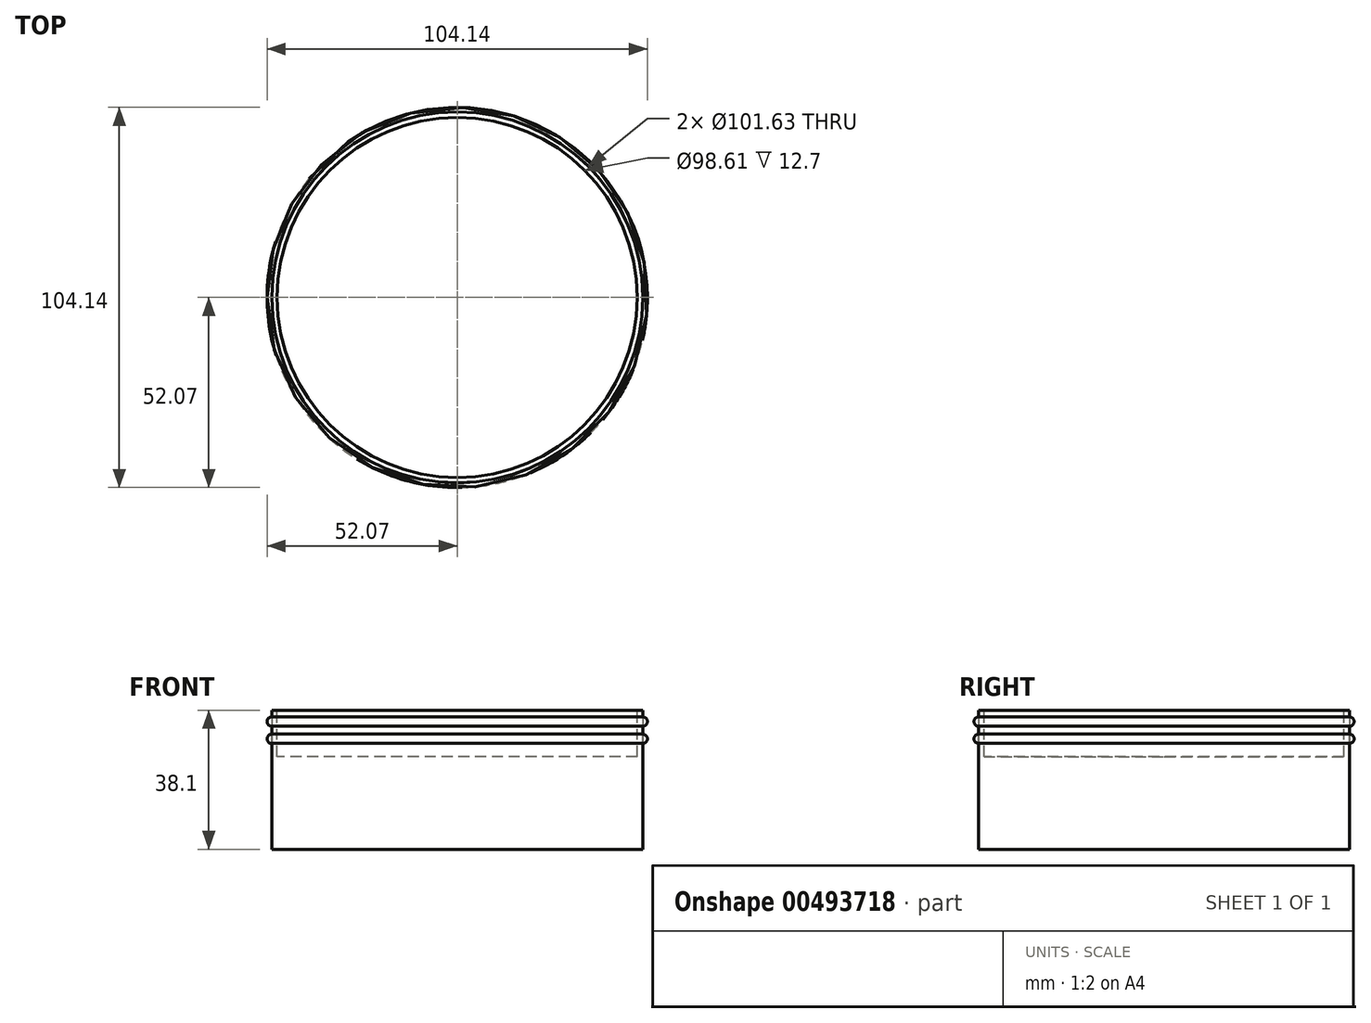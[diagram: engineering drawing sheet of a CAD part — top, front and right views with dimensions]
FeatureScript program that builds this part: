
annotation { "Feature Type Name" : "Feature", "Feature Type Description" : "" }
export const myFeature = defineFeature(function(context is Context, id is Id, definition is map)
    precondition{}
    {
        {
            var Q0;
            Q0=qCreatedBy(makeId("Top.planeOp"),FACE);
            var sketch = newSketch(context, id + "F0", { "sketchPlane" : qUnion([Q0])});
            skCircle(sketch, "E0", {"center": v(0, 0) * mm, "radius": 50.8 * mm});
            skSolve(sketch);
        }
        {
            var Q0;
            Q0 = qSketchRegion(id + "F0", true);
            extrude(context, id + "F1", {"entities" : qUnion([Q0]), "depth" : 38.1 * mm});
        }
        {
            var Q0;
            Q0=makeQuery(id+"F1.opExtrude","CAP_FACE",FACE,{"disambiguationData":[OSD([sQuery(id+"F0.wireOp",EDGE,"E0")])],"isStart":false});
            var sketch = newSketch(context, id + "F2", { "sketchPlane" : qUnion([Q0])});
            skCircle(sketch, "E1", {"center": v(0, 0) * mm, "radius": 49.3 * mm});
            skSolve(sketch);
        }
        {
            var Q0;
            Q0=makeQuery(id+"F2.imprint","IMPRINT",FACE,{"disambiguationData":[TD([[makeQuery(id+"F2.imprint","IMPRINT",EDGE,{"derivedFrom":sQuery(id+"F2.wireOp",EDGE,"E1")}),1.0]])]});
            extrude(context, id + "F3", {"entities" : qUnion([Q0]), "operationType" : NewBodyOperationType.REMOVE, "oppositeDirection" : true, "depth" : 12.7 * mm});
        }
        {
            var Q0;
            Q0=qCreatedBy(makeId("Front.planeOp"),FACE);
            var sketch = newSketch(context, id + "F4", { "sketchPlane" : qUnion([Q0])});
            skArc(sketch, "E2", {"start": v(50.82, 33.74) * mm, "mid": v(52.07, 35) * mm, "end": v(50.82, 36.28) * mm});
            skArc(sketch, "E3", {"start": v(50.82, 28.99) * mm, "mid": v(52.07, 30.26) * mm, "end": v(50.82, 31.53) * mm});
            skLineSegment(sketch, "E4", {"start": v(50.82, 36.28) * mm, "end": v(50.82, 28.99) * mm});
            skSolve(sketch);
        }
        {
            var Q0;
            {var subQ0=sQuery(id+"F4.wireOp",EDGE,"E2");Q0=makeQuery(id+"F4.imprint","IMPRINT",FACE,{"disambiguationData":[TD([[makeQuery(id+"F4.imprint","IMPRINT",EDGE,{"derivedFrom":subQ0}),1.0]])]});}
            var Q1;
            Q1=makeQuery(id+"F1.opExtrude","CAP_EDGE",EDGE,{"disambiguationData":[OSD([sQuery(id+"F0.wireOp",EDGE,"E0")])],"isStart":false});
            revolve(context, id + "F5", {"entities" : qUnion([Q0]), "axis" : qUnion([Q1]), "revolveType" : RevolveType.FULL});
        }
        {
            var Q0;
            {var subQ0=sQuery(id+"F4.wireOp",EDGE,"E3");Q0=makeQuery(id+"F4.imprint","IMPRINT",FACE,{"disambiguationData":[TD([[makeQuery(id+"F4.imprint","IMPRINT",EDGE,{"derivedFrom":subQ0}),1.0]])]});}
            var Q1;
            Q1=makeQuery(id+"F1.opExtrude","SWEPT_FACE",FACE,{"disambiguationData":[OSD([sQuery(id+"F0.wireOp",EDGE,"E0")])]});
            revolve(context, id + "F6", {"entities" : qUnion([Q0]), "axis" : qUnion([Q1]), "revolveType" : RevolveType.FULL});
        }
    });
